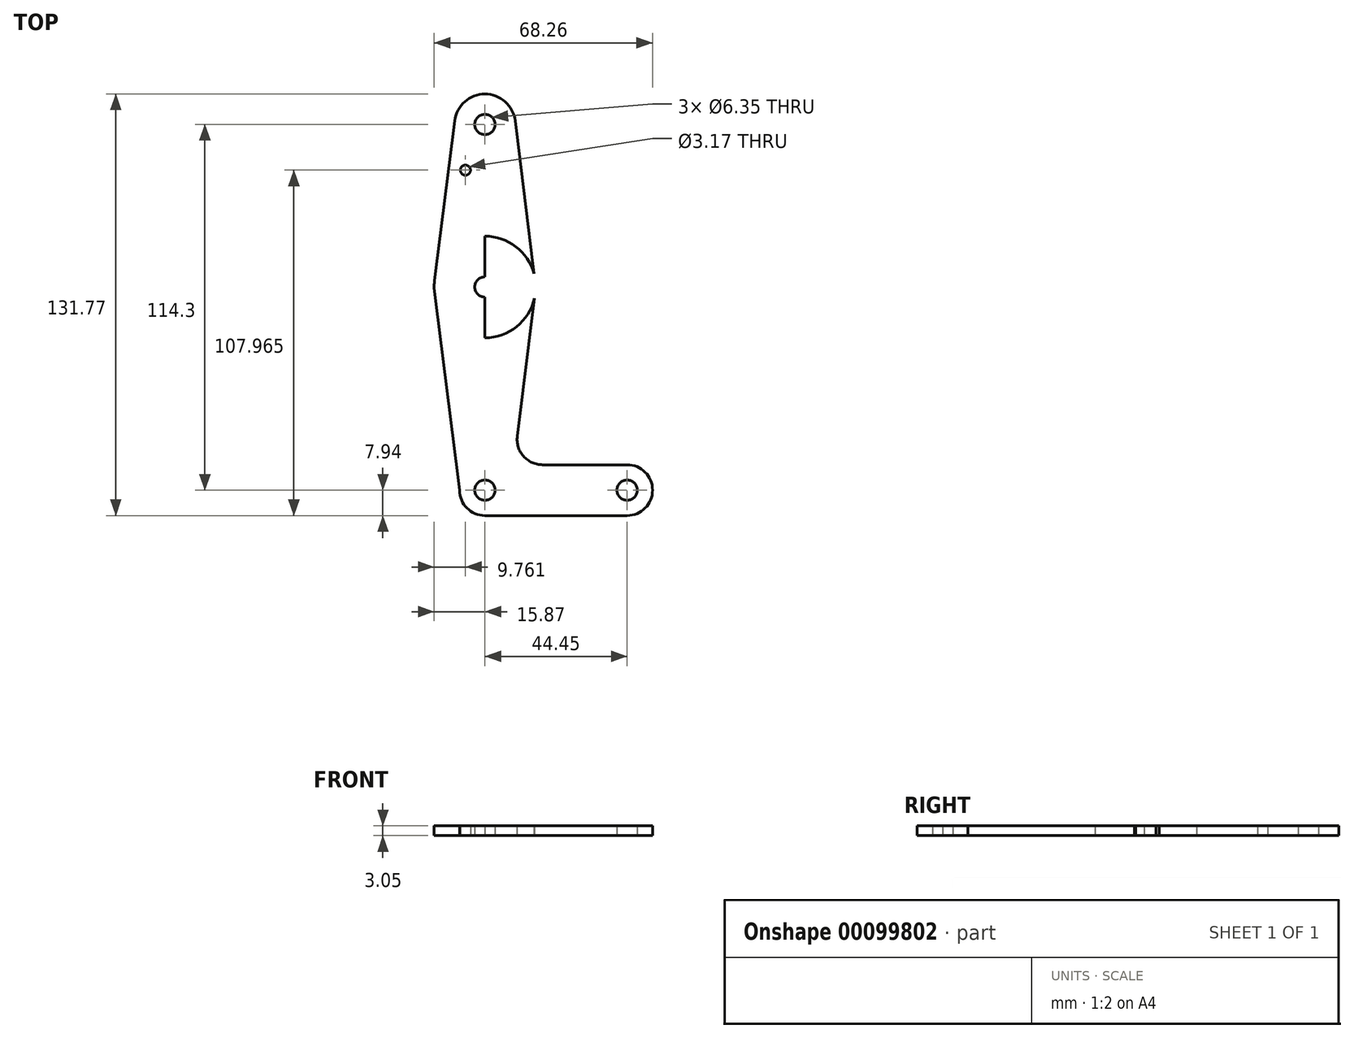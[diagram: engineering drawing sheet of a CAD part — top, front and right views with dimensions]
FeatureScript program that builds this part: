
annotation { "Feature Type Name" : "Feature", "Feature Type Description" : "" }
export const myFeature = defineFeature(function(context is Context, id is Id, definition is map)
    precondition{}
    {
        {
            var Q0;
            Q0=qCreatedBy(makeId("Top.planeOp"),FACE);
            var sketch = newSketch(context, id + "F0", { "sketchPlane" : qUnion([Q0])});
            skLineSegment(sketch, "E0", {"start": v(0, 114.3) * mm, "end": v(0, -1.4) * mm});
            skLineSegment(sketch, "E1", {"start": v(0, -1.4) * mm, "end": v(0, 0) * mm});
            skLineSegment(sketch, "E2", {"start": v(0, 0) * mm, "end": v(44.45, 0) * mm});
            skCircle(sketch, "E3", {"center": v(0, 114.3) * mm, "radius": 9.53 * mm});
            skCircle(sketch, "E4", {"center": v(0, 63.5) * mm, "radius": 15.88 * mm});
            skCircle(sketch, "E5", {"center": v(0, 0) * mm, "radius": 7.94 * mm});
            skCircle(sketch, "E6", {"center": v(44.45, 0) * mm, "radius": 7.94 * mm});
            skLineSegment(sketch, "E7", {"start": v(9.45, 115.46) * mm, "end": v(15.87, 63.1) * mm});
            skLineSegment(sketch, "E8", {"start": v(-9.45, 115.5) * mm, "end": v(-15.75, 65.48) * mm});
            skLineSegment(sketch, "E9", {"start": v(15.87, 63.1) * mm, "end": v(10.1, 16.87) * mm});
            skLineSegment(sketch, "E10", {"start": v(-15.87, 63.08) * mm, "end": v(-7.94, 0) * mm});
            skLineSegment(sketch, "E11", {"start": v(18, 7.94) * mm, "end": v(44.45, 7.94) * mm});
            skLineSegment(sketch, "E12", {"start": v(0, -7.94) * mm, "end": v(44.45, -7.94) * mm});
            skCircle(sketch, "E13", {"center": v(0, 114.3) * mm, "radius": 3.18 * mm});
            skCircle(sketch, "E14", {"center": v(0, 63.5) * mm, "radius": 3.18 * mm});
            skCircle(sketch, "E15", {"center": v(0, 0) * mm, "radius": 3.18 * mm});
            skCircle(sketch, "E16", {"center": v(44.45, 0) * mm, "radius": 3.18 * mm});
            skPoint(sketch, "E17.newPointA", {"position": v(8, 0) * mm});
            skPoint(sketch, "E17.newPointB", {"position": v(0, 7.94) * mm});
            skArc(sketch, "E17.filletArc", {"start": v(10.1, 16.87) * mm, "mid": v(12.03, 10.63) * mm, "end": v(18, 7.94) * mm});
            skCircle(sketch, "E18", {"center": v(-6.1, 100.03) * mm, "radius": 1.59 * mm});
            skSolve(sketch);
        }
        {
            var Q0;
            {var subQ0=sQuery(id+"F0.wireOp",EDGE,"E5");var subQ3=sQuery(id+"F0.wireOp",EDGE,"E0");var subQ4=makeQuery(id+"F0.imprint","INTERSECT",VERTEX,{"derivedFrom":[subQ3,subQ0]});Q0=makeQuery(id+"F0.imprint","IMPRINT",FACE,{"disambiguationData":[TD([[makeQuery(id+"F0.imprint","IMPRINT",EDGE,{"disambiguationData":[TD([[subQ4,-1.0]])],"derivedFrom":subQ3}),-1.0]])]});}
            var Q1;
            {var subQ0=sQuery(id+"F0.wireOp",EDGE,"E5");var subQ1=sQuery(id+"F0.wireOp",EDGE,"E0");var subQ2=makeQuery(id+"F0.imprint","INTERSECT",VERTEX,{"derivedFrom":[subQ1,subQ0]});Q1=makeQuery(id+"F0.imprint","IMPRINT",FACE,{"disambiguationData":[TD([[makeQuery(id+"F0.imprint","IMPRINT",EDGE,{"disambiguationData":[TD([[subQ2,-1.0]])],"derivedFrom":subQ1}),1.0]])]});}
            var Q2;
            {var subQ5=sQuery(id+"F0.wireOp",EDGE,"E11");Q2=makeQuery(id+"F0.imprint","IMPRINT",FACE,{"disambiguationData":[TD([[makeQuery(id+"F0.imprint","IMPRINT",EDGE,{"derivedFrom":subQ5}),-1.0]])]});}
            var Q3;
            {var subQ5=sQuery(id+"F0.wireOp",EDGE,"E12");Q3=makeQuery(id+"F0.imprint","IMPRINT",FACE,{"disambiguationData":[TD([[makeQuery(id+"F0.imprint","IMPRINT",EDGE,{"derivedFrom":subQ5}),1.0]])]});}
            var Q4;
            {var subQ0=sQuery(id+"F0.wireOp",EDGE,"E4");var subQ1=sQuery(id+"F0.wireOp",EDGE,"E0");var subQ2=makeQuery(id+"F0.imprint","INTERSECT",VERTEX,{"disambiguationData":[OD(1.0)],"derivedFrom":[subQ1,subQ0]});Q4=makeQuery(id+"F0.imprint","IMPRINT",FACE,{"disambiguationData":[TD([[makeQuery(id+"F0.imprint","IMPRINT",EDGE,{"disambiguationData":[TD([[subQ2,-1.0]])],"derivedFrom":subQ1}),-1.0]])]});}
            var Q5;
            Q5=makeQuery(id+"F0.imprint","IMPRINT",FACE,{"disambiguationData":[TD([[makeQuery(id+"F0.imprint","IMPRINT",EDGE,{"derivedFrom":sQuery(id+"F0.wireOp",EDGE,"E16")}),-1.0]])]});
            var Q6;
            {var subQ0=sQuery(id+"F0.wireOp",EDGE,"E4");var subQ4=sQuery(id+"F0.wireOp",EDGE,"E0");var subQ5=makeQuery(id+"F0.imprint","INTERSECT",VERTEX,{"disambiguationData":[OD(0.0)],"derivedFrom":[subQ4,subQ0]});Q6=makeQuery(id+"F0.imprint","IMPRINT",FACE,{"disambiguationData":[TD([[makeQuery(id+"F0.imprint","IMPRINT",EDGE,{"disambiguationData":[TD([[subQ5,-1.0]])],"derivedFrom":subQ4}),-1.0]])]});}
            var Q7;
            {var subQ1=sQuery(id+"F0.wireOp",EDGE,"E4");var subQ3=sQuery(id+"F0.wireOp",EDGE,"E0");var subQ4=makeQuery(id+"F0.imprint","INTERSECT",VERTEX,{"disambiguationData":[OD(0.0)],"derivedFrom":[subQ3,subQ1]});Q7=makeQuery(id+"F0.imprint","IMPRINT",FACE,{"disambiguationData":[TD([[makeQuery(id+"F0.imprint","IMPRINT",EDGE,{"disambiguationData":[TD([[subQ4,-1.0]])],"derivedFrom":subQ3}),1.0]])]});}
            var Q8;
            {var subQ0=sQuery(id+"F0.wireOp",EDGE,"E8");Q8=makeQuery(id+"F0.imprint","IMPRINT",FACE,{"disambiguationData":[TD([[makeQuery(id+"F0.imprint","IMPRINT",EDGE,{"derivedFrom":subQ0}),1.0]])]});}
            var Q9;
            {var subQ0=sQuery(id+"F0.wireOp",EDGE,"E3");var subQ1=sQuery(id+"F0.wireOp",EDGE,"E0");var subQ2=makeQuery(id+"F0.imprint","INTERSECT",VERTEX,{"derivedFrom":[subQ1,subQ0]});Q9=makeQuery(id+"F0.imprint","IMPRINT",FACE,{"disambiguationData":[TD([[makeQuery(id+"F0.imprint","IMPRINT",EDGE,{"disambiguationData":[TD([[subQ2,-1.0]])],"derivedFrom":subQ1}),1.0]])]});}
            var Q10;
            Q10=makeQuery(id+"F0.imprint","IMPRINT",FACE,{"disambiguationData":[TD([[makeQuery(id+"F0.imprint","IMPRINT",EDGE,{"derivedFrom":sQuery(id+"F0.wireOp",EDGE,"E13")}),-1.0]])]});
            extrude(context, id + "F1", {"entities" : qUnion([Q0, Q1, Q2, Q3, Q4, Q5, Q6, Q7, Q8, Q9, Q10]), "depth" : 3.05 * mm});
        }
    });
